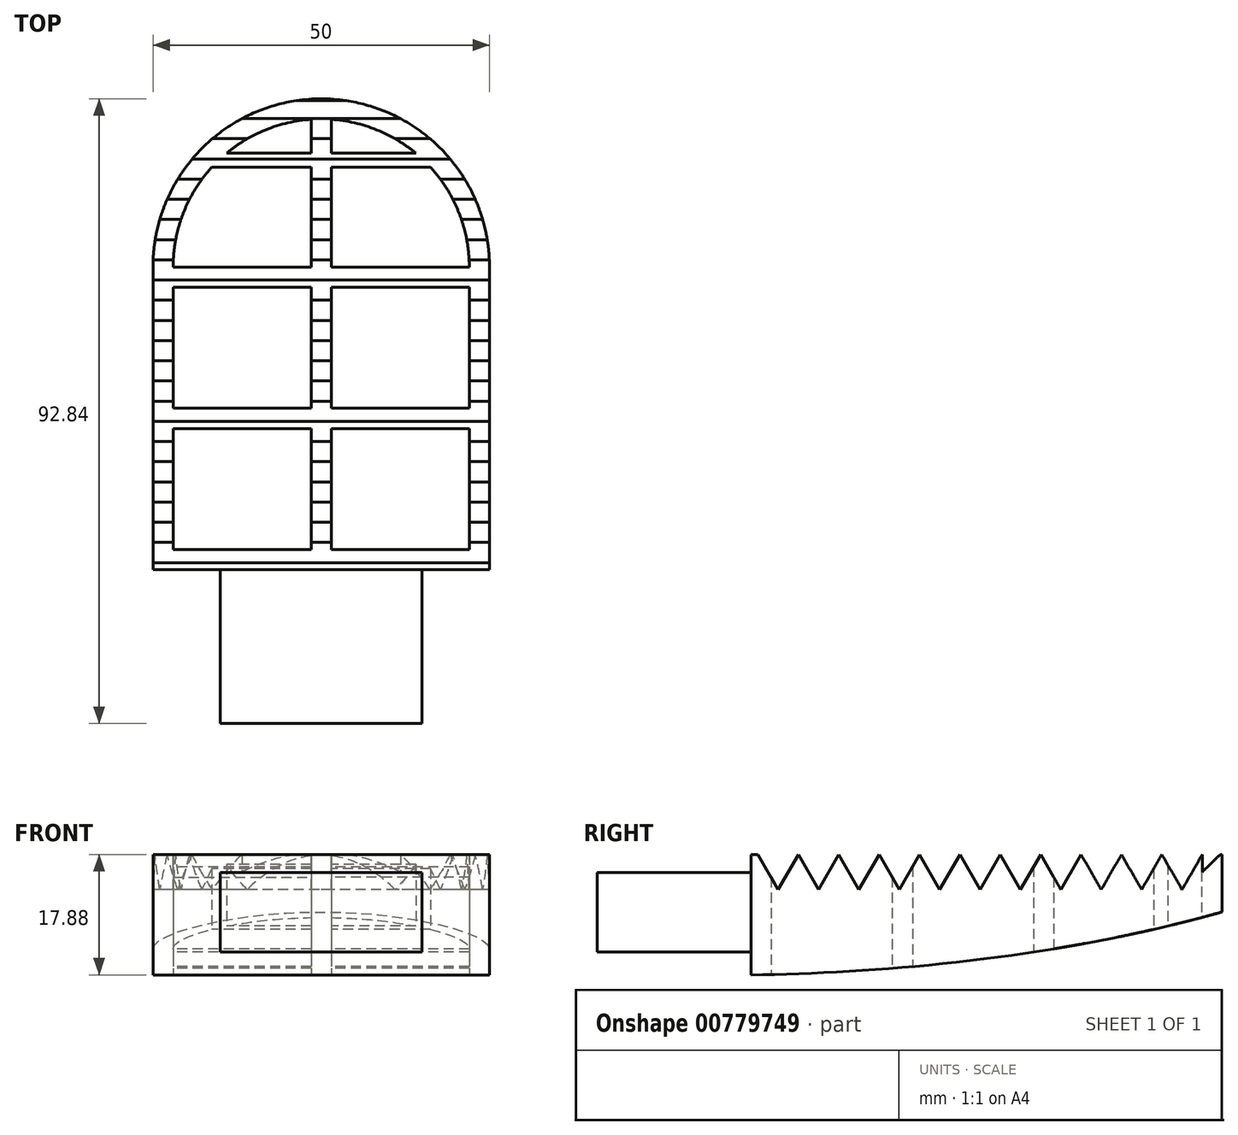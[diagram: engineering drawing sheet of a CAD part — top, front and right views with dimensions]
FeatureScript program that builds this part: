
annotation { "Feature Type Name" : "Feature", "Feature Type Description" : "" }
export const myFeature = defineFeature(function(context is Context, id is Id, definition is map)
    precondition{}
    {
        {
            var Q0;
            Q0=qCreatedBy(makeId("Top.planeOp"),FACE);
            var sketch = newSketch(context, id + "F0", { "sketchPlane" : qUnion([Q0])});
            skArc(sketch, "E0", {"start": v(-25, 0) * mm, "mid": v(0, 25) * mm, "end": v(25, 0) * mm});
            skLineSegment(sketch, "E1", {"start": v(-25, 0) * mm, "end": v(-25, -45) * mm});
            skLineSegment(sketch, "E2", {"start": v(25, 0) * mm, "end": v(25, -45) * mm});
            skLineSegment(sketch, "E3", {"start": v(-25, -45) * mm, "end": v(25, -45) * mm});
            skLineSegment(sketch, "E4", {"start": v(0, 25) * mm, "end": v(0, -45) * mm, "construction": true});
            skLineSegment(sketch, "E5", {"start": v(-25, -45) * mm, "end": v(-15, -45) * mm, "construction": true});
            skLineSegment(sketch, "E6.bottom", {"start": v(-15, -45) * mm, "end": v(15, -45) * mm});
            skLineSegment(sketch, "E6.top", {"start": v(-15, -67.84) * mm, "end": v(15, -67.84) * mm});
            skLineSegment(sketch, "E6.left", {"start": v(-15, -45) * mm, "end": v(-15, -67.84) * mm});
            skLineSegment(sketch, "E6.right", {"start": v(15, -45) * mm, "end": v(15, -67.84) * mm});
            skSolve(sketch);
        }
        {
            var Q0;
            Q0 = qSketchRegion(id + "F0", true);
            extrude(context, id + "F1", {"entities" : qUnion([Q0]), "depth" : 30 * mm, "offsetDistance" : 25 * mm});
        }
        {
            var Q0;
            Q0=makeQuery(id+"F1.opExtrude","SWEPT_FACE",FACE,{"disambiguationData":[OSD([sQuery(id+"F0.wireOp",EDGE,"E1")])]});
            var sketch = newSketch(context, id + "F2", { "sketchPlane" : qUnion([Q0])});
            skLineSegment(sketch, "E7", {"start": v(14.35, 0) * mm, "end": v(-25.66, 19.22) * mm});
            skLineSegment(sketch, "E8", {"start": v(-25.66, 19.22) * mm, "end": v(-25.66, 0) * mm});
            skLineSegment(sketch, "E9", {"start": v(-25.66, 0) * mm, "end": v(14.35, 0) * mm});
            skSolve(sketch);
        }
        {
            var Q0;
            {var subQ0=sQuery(id+"F2.wireOp",EDGE,"E8");Q0=makeQuery(id+"F2.imprint","IMPRINT",FACE,{"disambiguationData":[TD([[makeQuery(id+"F2.imprint","IMPRINT",EDGE,{"derivedFrom":subQ0}),1.0]])]});}
            var Q1;
            {var subQ0=sQuery(id+"F2.wireOp",EDGE,"E9");var subQ1=sQuery(id+"F2.wireOp",EDGE,"E7");var subQ2=sQuery(id+"F0.wireOp",EDGE,"E1");var subQ3=makeQuery(id+"F2.imprint","INTERSECT",VERTEX,{"derivedFrom":[makeQuery(id+"F1.opExtrude","CAP_EDGE",EDGE,{"disambiguationData":[OSD([subQ2])],"isStart":true}),subQ1,subQ0]});Q1=makeQuery(id+"F2.imprint","IMPRINT",FACE,{"disambiguationData":[TD([[makeQuery(id+"F2.imprint","IMPRINT",EDGE,{"disambiguationData":[TD([[subQ3,-1.0]])],"derivedFrom":subQ1}),1.0]])]});}
            extrude(context, id + "F3", {"entities" : qUnion([Q0, Q1]), "operationType" : NewBodyOperationType.REMOVE, "endBound" : BoundingType.THROUGH_ALL, "oppositeDirection" : true, "depth" : 25 * mm, "offsetDistance" : 25 * mm});
        }
        {
            var Q0;
            Q0=makeQuery(id+"F1.opExtrude","SWEPT_FACE",FACE,{"disambiguationData":[OSD([sQuery(id+"F0.wireOp",EDGE,"E1")])]});
            var sketch = newSketch(context, id + "F4", { "sketchPlane" : qUnion([Q0])});
            skLineSegment(sketch, "E10", {"start": v(43.94, 30) * mm, "end": v(40.94, 24.8) * mm});
            skLineSegment(sketch, "E11", {"start": v(40.94, 24.8) * mm, "end": v(37.94, 30) * mm});
            skLineSegment(sketch, "E12", {"start": v(37.94, 30) * mm, "end": v(43.94, 30) * mm});
            skLineSegment(sketch, "E13", {"start": v(37.94, 30) * mm, "end": v(34.94, 24.8) * mm});
            skLineSegment(sketch, "E14", {"start": v(34.94, 24.8) * mm, "end": v(31.94, 30) * mm});
            skLineSegment(sketch, "E15", {"start": v(31.94, 30) * mm, "end": v(37.94, 30) * mm});
            skLineSegment(sketch, "E16", {"start": v(31.94, 30) * mm, "end": v(28.94, 24.8) * mm});
            skLineSegment(sketch, "E17", {"start": v(28.94, 24.8) * mm, "end": v(25.94, 30) * mm});
            skLineSegment(sketch, "E18", {"start": v(25.94, 30) * mm, "end": v(31.94, 30) * mm});
            skLineSegment(sketch, "E19", {"start": v(25.94, 30) * mm, "end": v(22.94, 24.8) * mm});
            skLineSegment(sketch, "E20", {"start": v(22.94, 24.8) * mm, "end": v(19.94, 30) * mm});
            skLineSegment(sketch, "E21", {"start": v(19.94, 30) * mm, "end": v(25.94, 30) * mm});
            skLineSegment(sketch, "E22", {"start": v(19.94, 30) * mm, "end": v(16.94, 24.8) * mm});
            skLineSegment(sketch, "E23", {"start": v(16.94, 24.8) * mm, "end": v(13.94, 30) * mm});
            skLineSegment(sketch, "E24", {"start": v(13.94, 30) * mm, "end": v(19.94, 30) * mm});
            skLineSegment(sketch, "E25", {"start": v(13.94, 30) * mm, "end": v(10.94, 24.8) * mm});
            skLineSegment(sketch, "E26", {"start": v(10.94, 24.8) * mm, "end": v(7.94, 30) * mm});
            skLineSegment(sketch, "E27", {"start": v(7.94, 30) * mm, "end": v(13.94, 30) * mm});
            skLineSegment(sketch, "E28", {"start": v(7.94, 30) * mm, "end": v(4.94, 24.8) * mm});
            skLineSegment(sketch, "E29", {"start": v(4.94, 24.8) * mm, "end": v(1.94, 30) * mm});
            skLineSegment(sketch, "E30", {"start": v(1.94, 30) * mm, "end": v(7.94, 30) * mm});
            skLineSegment(sketch, "E31", {"start": v(1.94, 30) * mm, "end": v(-1.06, 24.8) * mm});
            skLineSegment(sketch, "E32", {"start": v(-1.06, 24.8) * mm, "end": v(-4.06, 30) * mm});
            skLineSegment(sketch, "E33", {"start": v(-4.06, 30) * mm, "end": v(1.94, 30) * mm});
            skLineSegment(sketch, "E34", {"start": v(-4.06, 30) * mm, "end": v(-7.06, 24.8) * mm});
            skLineSegment(sketch, "E35", {"start": v(-7.06, 24.8) * mm, "end": v(-10.06, 30) * mm});
            skLineSegment(sketch, "E36", {"start": v(-10.06, 30) * mm, "end": v(-4.06, 30) * mm});
            skLineSegment(sketch, "E37", {"start": v(-10.06, 30) * mm, "end": v(-13.06, 24.8) * mm});
            skLineSegment(sketch, "E38", {"start": v(-13.06, 24.8) * mm, "end": v(-16.06, 30) * mm});
            skLineSegment(sketch, "E39", {"start": v(-16.06, 30) * mm, "end": v(-10.06, 30) * mm});
            skLineSegment(sketch, "E40", {"start": v(-16.06, 30) * mm, "end": v(-19.06, 24.8) * mm});
            skLineSegment(sketch, "E41", {"start": v(-19.06, 24.8) * mm, "end": v(-22.06, 30) * mm});
            skLineSegment(sketch, "E42", {"start": v(-22.06, 30) * mm, "end": v(-16.06, 30) * mm});
            skLineSegment(sketch, "E43", {"start": v(-22.06, 30) * mm, "end": v(-22.06, 27.4) * mm});
            skPoint(sketch, "E43.endSnap0", {"position": v(-20.56, 27.4) * mm});
            skLineSegment(sketch, "E44", {"start": v(-22.06, 27.4) * mm, "end": v(-24.72, 30) * mm});
            skLineSegment(sketch, "E45", {"start": v(-24.72, 30) * mm, "end": v(-22.06, 30) * mm});
            skSolve(sketch);
        }
        {
            var Q0;
            Q0=makeQuery(id+"F4.imprint","IMPRINT",FACE,{"disambiguationData":[TD([[makeQuery(id+"F4.imprint","IMPRINT",EDGE,{"derivedFrom":sQuery(id+"F4.wireOp",EDGE,"E43")}),-1.0]])]});
            var Q1;
            Q1=makeQuery(id+"F4.imprint","IMPRINT",FACE,{"disambiguationData":[TD([[makeQuery(id+"F4.imprint","IMPRINT",EDGE,{"derivedFrom":sQuery(id+"F4.wireOp",EDGE,"E40")}),-1.0]])]});
            var Q2;
            Q2=makeQuery(id+"F4.imprint","IMPRINT",FACE,{"disambiguationData":[TD([[makeQuery(id+"F4.imprint","IMPRINT",EDGE,{"derivedFrom":sQuery(id+"F4.wireOp",EDGE,"E37")}),-1.0]])]});
            var Q3;
            Q3=makeQuery(id+"F4.imprint","IMPRINT",FACE,{"disambiguationData":[TD([[makeQuery(id+"F4.imprint","IMPRINT",EDGE,{"derivedFrom":sQuery(id+"F4.wireOp",EDGE,"E34")}),-1.0]])]});
            var Q4;
            {var subQ0=sQuery(id+"F4.wireOp",EDGE,"E32");Q4=makeQuery(id+"F4.imprint","IMPRINT",FACE,{"disambiguationData":[TD([[makeQuery(id+"F4.imprint","IMPRINT",EDGE,{"derivedFrom":subQ0}),-1.0]])]});}
            var Q5;
            {var subQ1=sQuery(id+"F4.wireOp",EDGE,"E31");var subQ3=makeQuery(id+"F1.opExtrude","SWEPT_EDGE",EDGE,{"disambiguationData":[OSD([sQuery(id+"F0.wireOp",EDGE,"E0"),sQuery(id+"F0.wireOp",EDGE,"E1")])]});var subQ4=makeQuery(id+"F4.imprint","INTERSECT",VERTEX,{"derivedFrom":[subQ3,subQ1]});Q5=makeQuery(id+"F4.imprint","IMPRINT",FACE,{"disambiguationData":[TD([[makeQuery(id+"F4.imprint","IMPRINT",EDGE,{"disambiguationData":[TD([[subQ4,1.0]])],"derivedFrom":subQ1}),-1.0]])]});}
            var Q6;
            Q6=makeQuery(id+"F4.imprint","IMPRINT",FACE,{"disambiguationData":[TD([[makeQuery(id+"F4.imprint","IMPRINT",EDGE,{"derivedFrom":sQuery(id+"F4.wireOp",EDGE,"E28")}),-1.0]])]});
            var Q7;
            Q7=makeQuery(id+"F4.imprint","IMPRINT",FACE,{"disambiguationData":[TD([[makeQuery(id+"F4.imprint","IMPRINT",EDGE,{"derivedFrom":sQuery(id+"F4.wireOp",EDGE,"E25")}),-1.0]])]});
            var Q8;
            Q8=makeQuery(id+"F4.imprint","IMPRINT",FACE,{"disambiguationData":[TD([[makeQuery(id+"F4.imprint","IMPRINT",EDGE,{"derivedFrom":sQuery(id+"F4.wireOp",EDGE,"E22")}),-1.0]])]});
            var Q9;
            Q9=makeQuery(id+"F4.imprint","IMPRINT",FACE,{"disambiguationData":[TD([[makeQuery(id+"F4.imprint","IMPRINT",EDGE,{"derivedFrom":sQuery(id+"F4.wireOp",EDGE,"E19")}),-1.0]])]});
            var Q10;
            Q10=makeQuery(id+"F4.imprint","IMPRINT",FACE,{"disambiguationData":[TD([[makeQuery(id+"F4.imprint","IMPRINT",EDGE,{"derivedFrom":sQuery(id+"F4.wireOp",EDGE,"E16")}),-1.0]])]});
            var Q11;
            Q11=makeQuery(id+"F4.imprint","IMPRINT",FACE,{"disambiguationData":[TD([[makeQuery(id+"F4.imprint","IMPRINT",EDGE,{"derivedFrom":sQuery(id+"F4.wireOp",EDGE,"E13")}),-1.0]])]});
            var Q12;
            Q12=makeQuery(id+"F4.imprint","IMPRINT",FACE,{"disambiguationData":[TD([[makeQuery(id+"F4.imprint","IMPRINT",EDGE,{"derivedFrom":sQuery(id+"F4.wireOp",EDGE,"E10")}),-1.0]])]});
            extrude(context, id + "F5", {"entities" : qUnion([Q0, Q1, Q2, Q3, Q4, Q5, Q6, Q7, Q8, Q9, Q10, Q11, Q12]), "operationType" : NewBodyOperationType.REMOVE, "endBound" : BoundingType.THROUGH_ALL, "oppositeDirection" : true, "depth" : 25 * mm, "offsetDistance" : 25 * mm});
        }
        {
            var Q0;
            Q0=qCreatedBy(makeId("Top.planeOp"),FACE);
            var sketch = newSketch(context, id + "F6", { "sketchPlane" : qUnion([Q0])});
            skArc(sketch, "E46", {"start": v(-22, 0) * mm, "mid": v(0, 22) * mm, "end": v(22, 0) * mm});
            skLineSegment(sketch, "E47", {"start": v(-22, 0) * mm, "end": v(-22, -42) * mm});
            skLineSegment(sketch, "E48", {"start": v(-22, -42) * mm, "end": v(22, -42) * mm});
            skLineSegment(sketch, "E49", {"start": v(22, -42) * mm, "end": v(22, 0) * mm});
            skLineSegment(sketch, "E50", {"start": v(-22, 0) * mm, "end": v(22, 0) * mm});
            skLineSegment(sketch, "E51", {"start": v(-22, -3) * mm, "end": v(22, -3) * mm});
            skLineSegment(sketch, "E52", {"start": v(-22, -21) * mm, "end": v(22, -21) * mm});
            skLineSegment(sketch, "E53", {"start": v(22, -21) * mm, "end": v(22, -24) * mm});
            skLineSegment(sketch, "E54", {"start": v(22, -24) * mm, "end": v(-22, -24) * mm});
            skLineSegment(sketch, "E55", {"start": v(-22, -24) * mm, "end": v(-22, -21) * mm});
            skLineSegment(sketch, "E56", {"start": v(-22, -3) * mm, "end": v(-22, 0) * mm});
            skLineSegment(sketch, "E57", {"start": v(22, 0) * mm, "end": v(22, -3) * mm});
            skLineSegment(sketch, "E58", {"start": v(-14.07, 16.91) * mm, "end": v(-16.24, 14.84) * mm});
            skLineSegment(sketch, "E59", {"start": v(-16.24, 14.84) * mm, "end": v(16.24, 14.84) * mm});
            skLineSegment(sketch, "E60", {"start": v(-14.07, 16.91) * mm, "end": v(14.07, 16.91) * mm});
            skLineSegment(sketch, "E61", {"start": v(14.07, 16.91) * mm, "end": v(16.24, 14.84) * mm});
            skLineSegment(sketch, "E62", {"start": v(0, 22) * mm, "end": v(1.5, 21.95) * mm});
            skLineSegment(sketch, "E63", {"start": v(1.5, 21.95) * mm, "end": v(1.5, -42) * mm});
            skLineSegment(sketch, "E64", {"start": v(1.5, -42) * mm, "end": v(0, -42) * mm});
            skLineSegment(sketch, "E65", {"start": v(0, -42) * mm, "end": v(0, 22) * mm});
            skLineSegment(sketch, "E66", {"start": v(0, 22) * mm, "end": v(-1.5, 21.95) * mm});
            skLineSegment(sketch, "E67", {"start": v(-1.5, 21.95) * mm, "end": v(-1.5, -42) * mm});
            skLineSegment(sketch, "E68", {"start": v(-1.5, -42) * mm, "end": v(0, -42) * mm});
            skSolve(sketch);
        }
        {
            var Q0;
            {var subQ0=sQuery(id+"F6.wireOp",EDGE,"E60");var subQ3=sQuery(id+"F6.wireOp",EDGE,"E63");var subQ5=makeQuery(id+"F6.imprint","INTERSECT",VERTEX,{"derivedFrom":[subQ0,subQ3]});Q0=makeQuery(id+"F6.imprint","IMPRINT",FACE,{"disambiguationData":[TD([[makeQuery(id+"F6.imprint","IMPRINT",EDGE,{"disambiguationData":[TD([[subQ5,-1.0]])],"derivedFrom":subQ0}),1.0]])]});}
            var Q1;
            {var subQ0=sQuery(id+"F6.wireOp",EDGE,"E60");var subQ3=sQuery(id+"F6.wireOp",EDGE,"E67");var subQ5=makeQuery(id+"F6.imprint","INTERSECT",VERTEX,{"derivedFrom":[subQ0,subQ3]});Q1=makeQuery(id+"F6.imprint","IMPRINT",FACE,{"disambiguationData":[TD([[makeQuery(id+"F6.imprint","IMPRINT",EDGE,{"disambiguationData":[TD([[subQ5,1.0]])],"derivedFrom":subQ0}),1.0]])]});}
            var Q2;
            {var subQ0=sQuery(id+"F6.wireOp",EDGE,"E50");var subQ5=sQuery(id+"F6.wireOp",EDGE,"E63");var subQ6=makeQuery(id+"F6.imprint","INTERSECT",VERTEX,{"derivedFrom":[subQ0,subQ5]});Q2=makeQuery(id+"F6.imprint","IMPRINT",FACE,{"disambiguationData":[TD([[makeQuery(id+"F6.imprint","IMPRINT",EDGE,{"disambiguationData":[TD([[subQ6,1.0]])],"derivedFrom":subQ5}),1.0]])]});}
            var Q3;
            {var subQ0=sQuery(id+"F6.wireOp",EDGE,"E50");var subQ5=sQuery(id+"F6.wireOp",EDGE,"E67");var subQ7=makeQuery(id+"F6.imprint","INTERSECT",VERTEX,{"derivedFrom":[subQ0,subQ5]});Q3=makeQuery(id+"F6.imprint","IMPRINT",FACE,{"disambiguationData":[TD([[makeQuery(id+"F6.imprint","IMPRINT",EDGE,{"disambiguationData":[TD([[subQ7,1.0]])],"derivedFrom":subQ5}),-1.0]])]});}
            var Q4;
            {var subQ0=sQuery(id+"F6.wireOp",EDGE,"E51");var subQ5=sQuery(id+"F6.wireOp",EDGE,"E67");var subQ6=makeQuery(id+"F6.imprint","INTERSECT",VERTEX,{"derivedFrom":[subQ0,subQ5]});Q4=makeQuery(id+"F6.imprint","IMPRINT",FACE,{"disambiguationData":[TD([[makeQuery(id+"F6.imprint","IMPRINT",EDGE,{"disambiguationData":[TD([[subQ6,-1.0]])],"derivedFrom":subQ5}),-1.0]])]});}
            var Q5;
            {var subQ0=sQuery(id+"F6.wireOp",EDGE,"E48");var subQ1=sQuery(id+"F6.wireOp",EDGE,"E47");var subQ2=makeQuery(id+"F6.imprint","INTERSECT",VERTEX,{"derivedFrom":[subQ1,subQ0]});Q5=makeQuery(id+"F6.imprint","IMPRINT",FACE,{"disambiguationData":[TD([[makeQuery(id+"F6.imprint","IMPRINT",EDGE,{"disambiguationData":[TD([[subQ2,1.0]])],"derivedFrom":subQ1}),1.0]])]});}
            var Q6;
            {var subQ0=sQuery(id+"F6.wireOp",EDGE,"E51");var subQ5=sQuery(id+"F6.wireOp",EDGE,"E63");var subQ6=makeQuery(id+"F6.imprint","INTERSECT",VERTEX,{"derivedFrom":[subQ0,subQ5]});Q6=makeQuery(id+"F6.imprint","IMPRINT",FACE,{"disambiguationData":[TD([[makeQuery(id+"F6.imprint","IMPRINT",EDGE,{"disambiguationData":[TD([[subQ6,-1.0]])],"derivedFrom":subQ5}),1.0]])]});}
            var Q7;
            {var subQ0=sQuery(id+"F6.wireOp",EDGE,"E49");var subQ1=sQuery(id+"F6.wireOp",EDGE,"E48");var subQ2=makeQuery(id+"F6.imprint","INTERSECT",VERTEX,{"derivedFrom":[subQ1,subQ0]});Q7=makeQuery(id+"F6.imprint","IMPRINT",FACE,{"disambiguationData":[TD([[makeQuery(id+"F6.imprint","IMPRINT",EDGE,{"disambiguationData":[TD([[subQ2,1.0]])],"derivedFrom":subQ1}),1.0]])]});}
            extrude(context, id + "F7", {"entities" : qUnion([Q0, Q1, Q2, Q3, Q4, Q5, Q6, Q7]), "operationType" : NewBodyOperationType.REMOVE, "endBound" : BoundingType.THROUGH_ALL, "depth" : 25 * mm, "offsetDistance" : 25 * mm});
        }
        {
            var Q0;
            Q0=makeQuery(id+"F1.opExtrude","SWEPT_FACE",FACE,{"disambiguationData":[OSD([sQuery(id+"F0.wireOp",EDGE,"E1")])]});
            var sketch = newSketch(context, id + "F8", { "sketchPlane" : qUnion([Q0])});
            skLineSegment(sketch, "E69", {"start": v(14.35, 0) * mm, "end": v(0, 6.9) * mm});
            skLineSegment(sketch, "E70", {"start": v(0, 6.9) * mm, "end": v(68.69, 6.9) * mm});
            skLineSegment(sketch, "E71", {"start": v(68.69, 6.9) * mm, "end": v(68.69, 0) * mm});
            skLineSegment(sketch, "E72", {"start": v(68.69, 0) * mm, "end": v(14.35, 0) * mm});
            skSolve(sketch);
        }
        {
            var Q0;
            {var subQ0=sQuery(id+"F8.wireOp",EDGE,"E71");Q0=makeQuery(id+"F8.imprint","IMPRINT",FACE,{"disambiguationData":[TD([[makeQuery(id+"F8.imprint","IMPRINT",EDGE,{"derivedFrom":subQ0}),-1.0]])]});}
            var Q1;
            {var subQ0=sQuery(id+"F8.wireOp",EDGE,"E69");Q1=makeQuery(id+"F8.imprint","IMPRINT",FACE,{"disambiguationData":[TD([[makeQuery(id+"F8.imprint","IMPRINT",EDGE,{"derivedFrom":subQ0}),-1.0]])]});}
            extrude(context, id + "F9", {"entities" : qUnion([Q0, Q1]), "operationType" : NewBodyOperationType.REMOVE, "endBound" : BoundingType.THROUGH_ALL, "oppositeDirection" : true, "depth" : 25 * mm, "offsetDistance" : 25 * mm});
        }
        {
            var Q0;
            Q0=makeQuery(id+"F1.opExtrude","SWEPT_FACE",FACE,{"disambiguationData":[OSD([sQuery(id+"F0.wireOp",EDGE,"E1")])]});
            var sketch = newSketch(context, id + "F10", { "sketchPlane" : qUnion([Q0])});
            skFitSpline(sketch, "E73", {"points": [v(-25.46, 21.6) * mm, v(45, 12.12) * mm], "startDerivative": vector(72.4, -20.62) * mm, "endDerivative": vector(60.65, -0.8) * mm});
            skLineSegment(sketch, "E74", {"start": v(-25.46, 21.6) * mm, "end": v(-25.46, 18.73) * mm});
            skLineSegment(sketch, "E75", {"start": v(-25.46, 18.73) * mm, "end": v(0, 6.9) * mm});
            skLineSegment(sketch, "E76", {"start": v(0, 6.9) * mm, "end": v(45, 6.9) * mm});
            skLineSegment(sketch, "E77", {"start": v(45, 6.9) * mm, "end": v(45, 12.12) * mm});
            skSolve(sketch);
        }
        {
            var Q0;
            Q0 = qSketchRegion(id + "F10", true);
            extrude(context, id + "F11", {"entities" : qUnion([Q0]), "operationType" : NewBodyOperationType.REMOVE, "endBound" : BoundingType.THROUGH_ALL, "oppositeDirection" : true, "depth" : 25 * mm, "offsetDistance" : 25 * mm});
        }
        {
            var Q0;
            Q0=makeQuery(id+"F1.opExtrude","SWEPT_FACE",FACE,{"disambiguationData":[OSD([sQuery(id+"F0.wireOp",EDGE,"E6.left")])]});
            var sketch = newSketch(context, id + "F12", { "sketchPlane" : qUnion([Q0])});
            skLineSegment(sketch, "E78", {"start": v(45, 15.5) * mm, "end": v(67.84, 15.5) * mm});
            skLineSegment(sketch, "E79", {"start": v(67.84, 15.5) * mm, "end": v(67.84, 6.9) * mm});
            skLineSegment(sketch, "E80", {"start": v(67.84, 6.9) * mm, "end": v(45, 6.9) * mm});
            skLineSegment(sketch, "E81", {"start": v(45, 6.9) * mm, "end": v(45, 15.5) * mm});
            skLineSegment(sketch, "E82", {"start": v(45, 30) * mm, "end": v(67.84, 30) * mm});
            skLineSegment(sketch, "E83", {"start": v(67.84, 30) * mm, "end": v(67.84, 27.36) * mm});
            skLineSegment(sketch, "E84", {"start": v(67.84, 27.36) * mm, "end": v(45, 27.36) * mm});
            skLineSegment(sketch, "E85", {"start": v(45, 27.36) * mm, "end": v(45, 30) * mm});
            skSolve(sketch);
        }
        {
            var Q0;
            Q0=makeQuery(id+"F12.imprint","IMPRINT",FACE,{"disambiguationData":[TD([[makeQuery(id+"F12.imprint","IMPRINT",EDGE,{"derivedFrom":sQuery(id+"F12.wireOp",EDGE,"E82")}),-1.0]])]});
            var Q1;
            {var subQ2=sQuery(id+"F12.wireOp",EDGE,"E78");Q1=makeQuery(id+"F12.imprint","IMPRINT",FACE,{"disambiguationData":[TD([[makeQuery(id+"F12.imprint","IMPRINT",EDGE,{"derivedFrom":subQ2}),-1.0]])]});}
            extrude(context, id + "F13", {"entities" : qUnion([Q0, Q1]), "operationType" : NewBodyOperationType.REMOVE, "endBound" : BoundingType.THROUGH_ALL, "oppositeDirection" : true, "depth" : 25 * mm, "offsetDistance" : 25 * mm});
        }
    });
